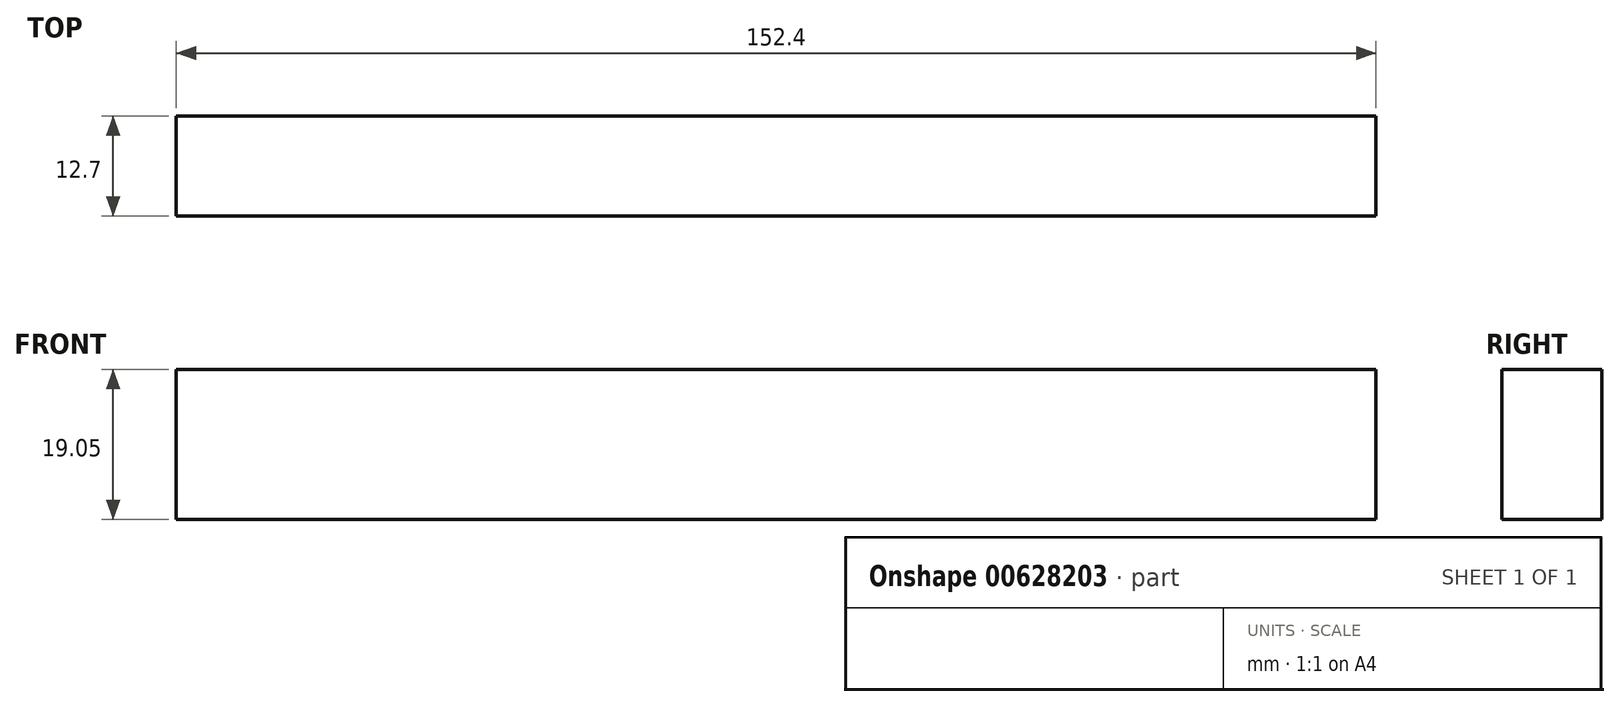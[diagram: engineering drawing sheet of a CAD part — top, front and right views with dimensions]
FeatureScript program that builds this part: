
annotation { "Feature Type Name" : "Feature", "Feature Type Description" : "" }
export const myFeature = defineFeature(function(context is Context, id is Id, definition is map)
    precondition{}
    {
        {
            var Q0;
            Q0=qCreatedBy(makeId("Front.planeOp"),FACE);
            var sketch = newSketch(context, id + "F0", { "sketchPlane" : qUnion([Q0])});
            skLineSegment(sketch, "E0.bottom", {"start": v(0, 0) * mm, "end": v(152.4, 0) * mm});
            skLineSegment(sketch, "E0.top", {"start": v(0, 19.05) * mm, "end": v(152.4, 19.05) * mm});
            skLineSegment(sketch, "E0.left", {"start": v(0, 0) * mm, "end": v(0, 19.05) * mm});
            skLineSegment(sketch, "E0.right", {"start": v(152.4, 0) * mm, "end": v(152.4, 19.05) * mm});
            skSolve(sketch);
        }
        {
            var Q0;
            Q0=qSketchRegion(id+"F0",true);
            extrude(context, id + "F1", {"entities" : qUnion([Q0]), "depth" : 12.7 * mm, "offsetDistance" : 25.4 * mm});
        }
    });
